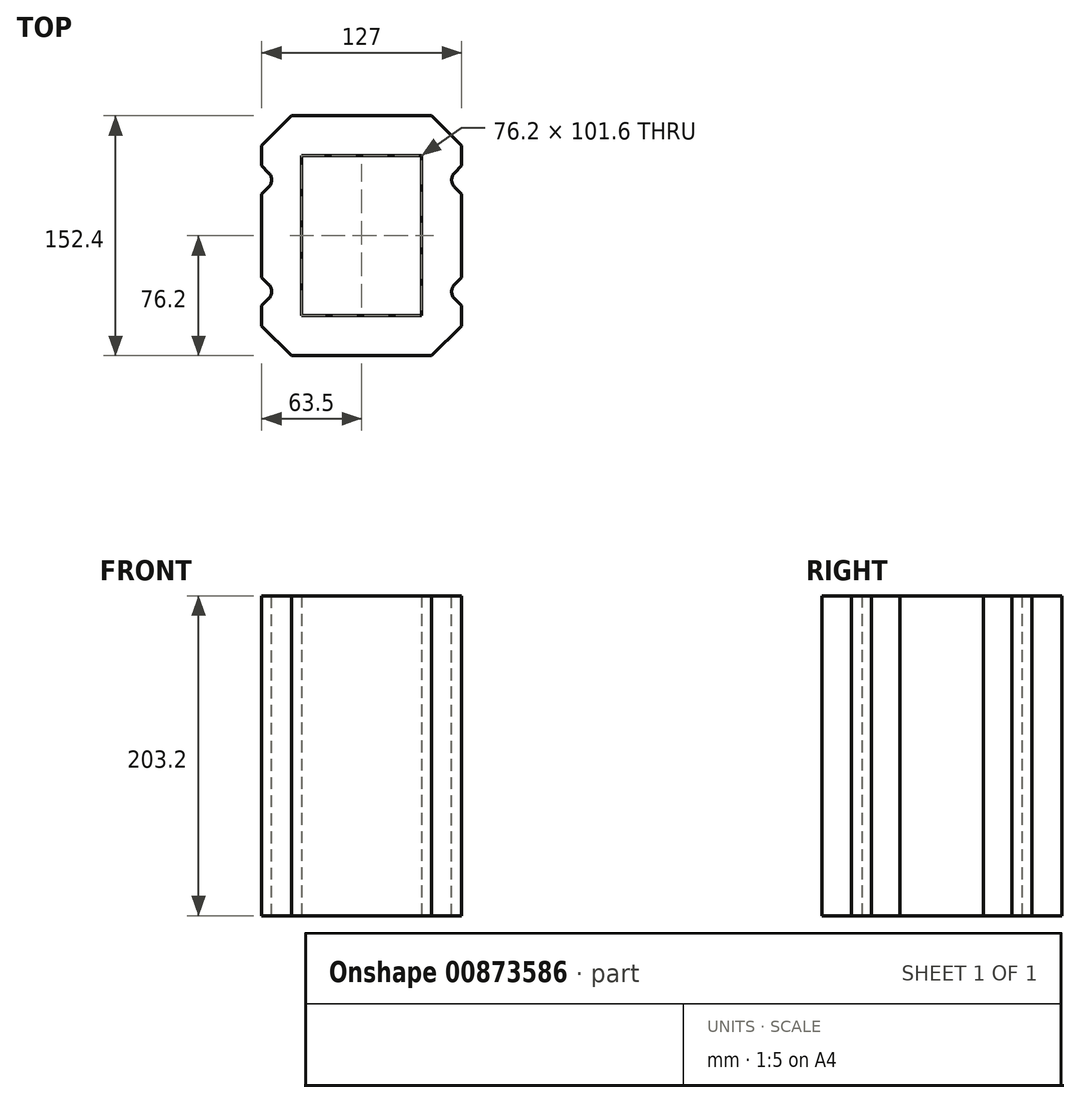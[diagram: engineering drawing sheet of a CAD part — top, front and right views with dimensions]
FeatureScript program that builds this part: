
annotation { "Feature Type Name" : "Feature", "Feature Type Description" : "" }
export const myFeature = defineFeature(function(context is Context, id is Id, definition is map)
    precondition{}
    {
        {
            var Q0;
            Q0=qCreatedBy(makeId("Top.planeOp"),FACE);
            var sketch = newSketch(context, id + "F0", { "sketchPlane" : qUnion([Q0])});
            skLineSegment(sketch, "E0.bottom", {"start": v(19.04, 0) * mm, "end": v(107.96, 0) * mm});
            skLineSegment(sketch, "E0.top", {"start": v(19.04, 152.4) * mm, "end": v(107.96, 152.4) * mm});
            skLineSegment(sketch, "E0.left", {"start": v(0, 19) * mm, "end": v(0, 31.73) * mm});
            skLineSegment(sketch, "E0.right", {"start": v(127, 19) * mm, "end": v(127, 31.73) * mm});
            skLineSegment(sketch, "E1.0", {"start": v(25.4, 25.4) * mm, "end": v(101.6, 25.4) * mm});
            skLineSegment(sketch, "E1.1", {"start": v(25.4, 25.4) * mm, "end": v(25.4, 127) * mm});
            skLineSegment(sketch, "E1.2", {"start": v(25.4, 127) * mm, "end": v(101.6, 127) * mm});
            skLineSegment(sketch, "E1.3", {"start": v(101.6, 25.4) * mm, "end": v(101.6, 127) * mm});
            skLineSegment(sketch, "E2", {"start": v(127, 120.67) * mm, "end": v(118.01, 111.67) * mm});
            skLineSegment(sketch, "E3", {"start": v(118.01, 111.67) * mm, "end": v(127, 102.7) * mm});
            skLineSegment(sketch, "E4", {"start": v(127, 120.67) * mm, "end": v(127, 133.4) * mm});
            skLineSegment(sketch, "E5", {"start": v(127, 133.4) * mm, "end": v(107.96, 152.4) * mm});
            skLineSegment(sketch, "E6", {"start": v(63.5, 127) * mm, "end": v(63.5, 527.51) * mm, "construction": true});
            skLineSegment(sketch, "E7.MirrorCS", {"start": v(0, 133.4) * mm, "end": v(19.04, 152.4) * mm});
            skLineSegment(sketch, "E8.MirrorCS", {"start": v(0, 120.67) * mm, "end": v(0, 133.4) * mm});
            skLineSegment(sketch, "E9.MirrorCS", {"start": v(0, 120.67) * mm, "end": v(8.99, 111.67) * mm});
            skLineSegment(sketch, "E10.MirrorCS", {"start": v(8.99, 111.67) * mm, "end": v(0, 102.7) * mm});
            skLineSegment(sketch, "E11", {"start": v(101.6, 76.2) * mm, "end": v(288.26, 76.2) * mm, "construction": true});
            skLineSegment(sketch, "E12.MirrorCS", {"start": v(0, 19) * mm, "end": v(19.04, 0) * mm});
            skLineSegment(sketch, "E13.MirrorCS", {"start": v(0, 31.73) * mm, "end": v(8.99, 40.73) * mm});
            skLineSegment(sketch, "E14.MirrorCS", {"start": v(8.99, 40.73) * mm, "end": v(0, 49.7) * mm});
            skLineSegment(sketch, "E15.MirrorCS", {"start": v(127, 19) * mm, "end": v(107.96, 0) * mm});
            skLineSegment(sketch, "E16.MirrorCS", {"start": v(127, 31.73) * mm, "end": v(118.01, 40.73) * mm});
            skLineSegment(sketch, "E17.MirrorCS", {"start": v(118.01, 40.73) * mm, "end": v(127, 49.7) * mm});
            skLineSegment(sketch, "E18.trimOffspring", {"start": v(127, 49.7) * mm, "end": v(127, 102.7) * mm});
            skLineSegment(sketch, "E19.trimOffspring", {"start": v(0, 49.7) * mm, "end": v(0, 102.7) * mm});
            skSolve(sketch);
        }
        {
            var Q0;
            Q0=qSketchRegion(id+"F0",true);
            extrude(context, id + "F1", {"entities" : qUnion([Q0]), "depth" : 203.2 * mm, "offsetDistance" : 25.4 * mm});
        }
        {
            var Q0;
            Q0=makeQuery(id+"F1.opExtrude","SWEPT_EDGE",EDGE,{"disambiguationData":[OSD([sQuery(id+"F0.wireOp",EDGE,"E2"),sQuery(id+"F0.wireOp",EDGE,"E3")])]});
            var Q1;
            Q1=makeQuery(id+"F1.opExtrude","SWEPT_EDGE",EDGE,{"disambiguationData":[OSD([sQuery(id+"F0.wireOp",EDGE,"E9.MirrorCS"),sQuery(id+"F0.wireOp",EDGE,"E10.MirrorCS")])]});
            var Q2;
            Q2=makeQuery(id+"F1.opExtrude","SWEPT_EDGE",EDGE,{"disambiguationData":[OSD([sQuery(id+"F0.wireOp",EDGE,"E13.MirrorCS"),sQuery(id+"F0.wireOp",EDGE,"E14.MirrorCS")])]});
            var Q3;
            Q3=makeQuery(id+"F1.opExtrude","SWEPT_EDGE",EDGE,{"disambiguationData":[OSD([sQuery(id+"F0.wireOp",EDGE,"E16.MirrorCS"),sQuery(id+"F0.wireOp",EDGE,"E17.MirrorCS")])]});
            fillet(context, id + "F2", {"entities" : qUnion([Q0, Q1, Q2, Q3]), "radius" : 6.35 * mm, "tangentPropagation" : true, "allowEdgeOverflow" : false});
        }
    });
